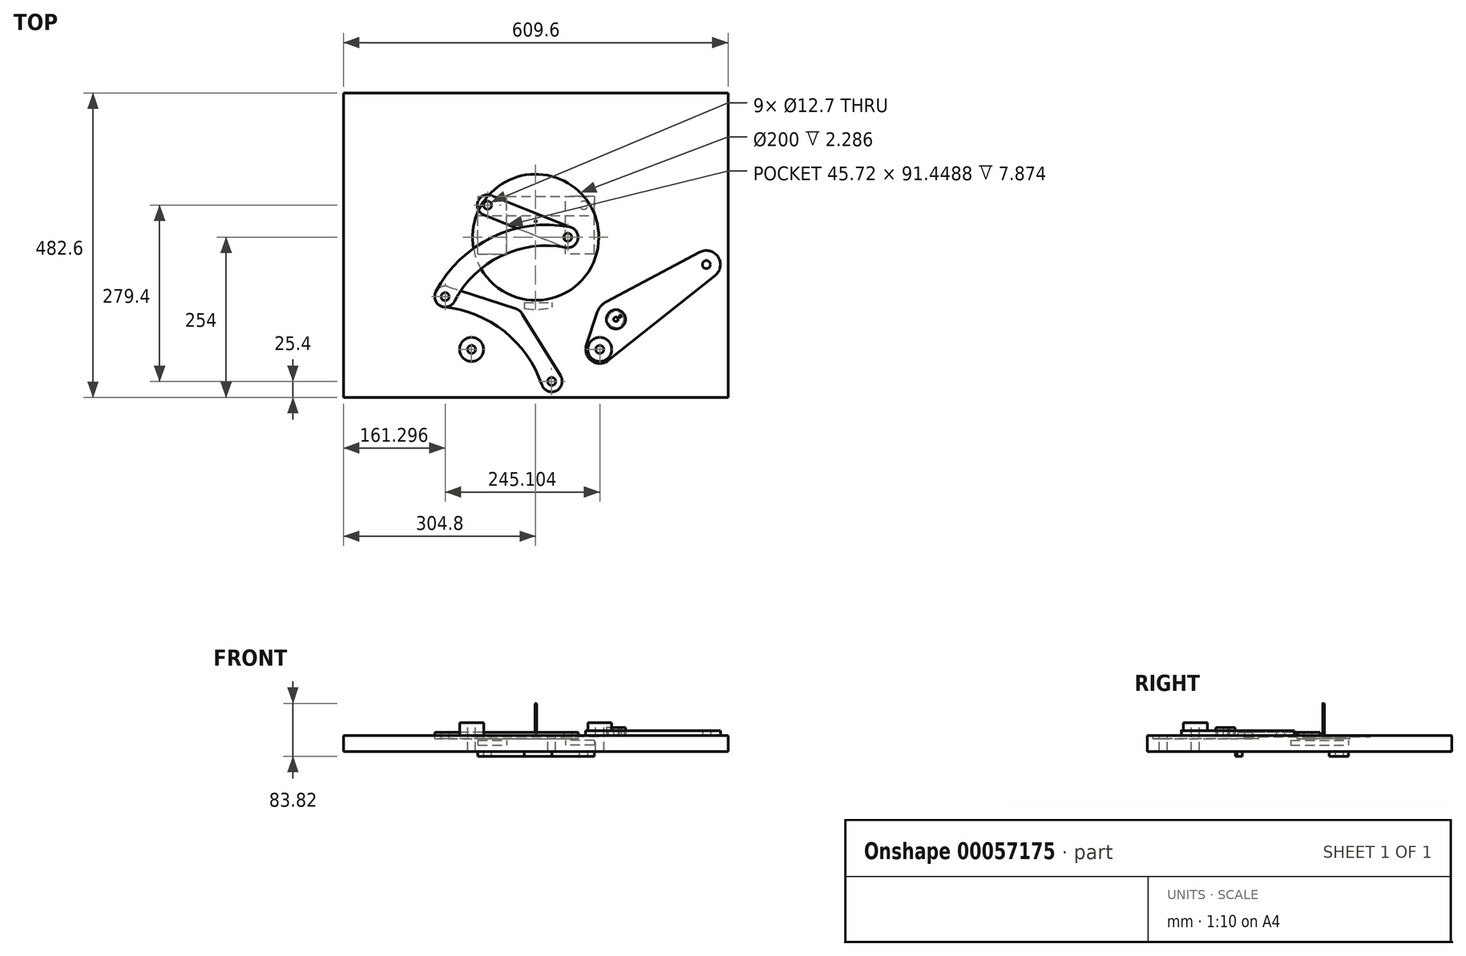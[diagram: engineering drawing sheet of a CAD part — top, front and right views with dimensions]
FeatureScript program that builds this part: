
annotation { "Feature Type Name" : "Feature", "Feature Type Description" : "" }
export const myFeature = defineFeature(function(context is Context, id is Id, definition is map)
    precondition{}
    {
        {
            var Q0;
            Q0=qCreatedBy(makeId("Top.planeOp"),FACE);
            var sketch = newSketch(context, id + "F0", { "sketchPlane" : qUnion([Q0])});
            skCircle(sketch, "E0", {"center": v(0, 0) * mm, "radius": 101.6 * mm, "construction": true});
            skLineSegment(sketch, "E1", {"start": v(-76.2, 50.8) * mm, "end": v(-76.2, 0) * mm, "construction": true});
            skPoint(sketch, "E2", {"position": v(-101.6, -177.8) * mm});
            skCircle(sketch, "E3", {"center": v(-76.2, 50.8) * mm, "radius": 6.35 * mm});
            skLineSegment(sketch, "E4", {"start": v(0, 0) * mm, "end": v(50.8, 0) * mm, "construction": true});
            skCircle(sketch, "E5", {"center": v(50.8, 0) * mm, "radius": 6.35 * mm});
            skPoint(sketch, "E6", {"position": v(25.4, -228.6) * mm});
            skCircle(sketch, "E7", {"center": v(-101.6, -177.8) * mm, "radius": 6.35 * mm});
            skCircle(sketch, "E8", {"center": v(25.4, -228.6) * mm, "radius": 6.35 * mm});
            skLineSegment(sketch, "E9", {"start": v(0, 0) * mm, "end": v(0, 167.48) * mm, "construction": true});
            skCircle(sketch, "E10.MirrorC", {"center": v(76.2, 50.8) * mm, "radius": 6.35 * mm});
            skCircle(sketch, "E11.MirrorC", {"center": v(-50.8, 0) * mm, "radius": 6.35 * mm});
            skCircle(sketch, "E12.MirrorC", {"center": v(101.6, -177.8) * mm, "radius": 6.35 * mm});
            skLineSegment(sketch, "E13", {"start": v(-76.2, 50.8) * mm, "end": v(-270.5, -43.32) * mm});
            skLineSegment(sketch, "E14", {"start": v(-270.5, -43.32) * mm, "end": v(-101.6, -177.8) * mm});
            skLineSegment(sketch, "E15", {"start": v(76.2, 50.8) * mm, "end": v(270.5, -43.32) * mm});
            skLineSegment(sketch, "E16", {"start": v(270.5, -43.32) * mm, "end": v(101.6, -177.8) * mm});
            skLineSegment(sketch, "E17", {"start": v(50.8, 0) * mm, "end": v(-143.5, -94.12) * mm});
            skLineSegment(sketch, "E18", {"start": v(-143.5, -94.12) * mm, "end": v(25.4, -228.6) * mm});
            skArc(sketch, "E19", {"start": v(133.35, 23.12) * mm, "mid": v(131.45, -105.68) * mm, "end": v(228.9, -189.93) * mm});
            skLineSegment(sketch, "E20", {"start": v(270.5, -43.32) * mm, "end": v(228.9, -189.93) * mm});
            skCircle(sketch, "E21", {"center": v(127.1, -130.13) * mm, "radius": 15.24 * mm});
            skLineSegment(sketch, "E22", {"start": v(270.5, -43.32) * mm, "end": v(127.1, -130.13) * mm, "construction": true});
            skLineSegment(sketch, "E23", {"start": v(127.1, -130.13) * mm, "end": v(101.6, -177.8) * mm, "construction": true});
            skLineSegment(sketch, "E24", {"start": v(-76.2, 50.8) * mm, "end": v(50.8, 0) * mm});
            skSolve(sketch);
        }
        {
            var Q0;
            Q0=qCreatedBy(makeId("Top.planeOp"),FACE);
            var sketch = newSketch(context, id + "F1", { "sketchPlane" : qUnion([Q0])});
            skCircle(sketch, "E25", {"center": v(76.2, 50.8) * mm, "radius": 22.23 * mm});
            skCircle(sketch, "E26", {"center": v(270.5, -43.32) * mm, "radius": 22.23 * mm});
            skLineSegment(sketch, "E27", {"start": v(85.89, 70.8) * mm, "end": v(280.2, -23.32) * mm});
            skLineSegment(sketch, "E28", {"start": v(291.88, -49.4) * mm, "end": v(250.72, -194.43) * mm});
            skArc(sketch, "E29", {"start": v(120.43, -16.82) * mm, "mid": v(147.62, -133.46) * mm, "end": v(250.72, -194.43) * mm});
            skLineSegment(sketch, "E30", {"start": v(61.66, 33.99) * mm, "end": v(120.43, -16.82) * mm});
            skCircle(sketch, "E31", {"center": v(270.5, -43.32) * mm, "radius": 6.35 * mm});
            skCircle(sketch, "E32", {"center": v(76.2, 50.8) * mm, "radius": 6.35 * mm});
            skSolve(sketch);
        }
        {
            var Q0;
            Q0=qCreatedBy(makeId("Top.planeOp"),FACE);
            var sketch = newSketch(context, id + "F2", { "sketchPlane" : qUnion([Q0])});
            skCircle(sketch, "E33", {"center": v(270.5, -43.32) * mm, "radius": 22.23 * mm});
            skCircle(sketch, "E34", {"center": v(101.6, -177.8) * mm, "radius": 22.23 * mm});
            skCircle(sketch, "E35", {"center": v(127.1, -130.13) * mm, "radius": 31.75 * mm});
            skLineSegment(sketch, "E36", {"start": v(260.1, -23.69) * mm, "end": v(112.22, -102.08) * mm});
            skLineSegment(sketch, "E37", {"start": v(284.35, -60.7) * mm, "end": v(115.44, -195.19) * mm});
            skLineSegment(sketch, "E38", {"start": v(96.9, -120.33) * mm, "end": v(80.46, -170.94) * mm});
            skCircle(sketch, "E39", {"center": v(270.5, -43.32) * mm, "radius": 6.35 * mm});
            skCircle(sketch, "E40", {"center": v(101.6, -177.8) * mm, "radius": 6.35 * mm});
            skCircle(sketch, "E41", {"center": v(127.1, -130.13) * mm, "radius": 12.7 * mm});
            skSolve(sketch);
        }
        {
            var Q0;
            Q0=qCreatedBy(makeId("Top.planeOp"),FACE);
            var sketch = newSketch(context, id + "F3", { "sketchPlane" : qUnion([Q0])});
            skCircle(sketch, "E42", {"center": v(0, 0) * mm, "radius": 114.3 * mm});
            skCircle(sketch, "E43", {"center": v(-76.2, 50.8) * mm, "radius": 12.31 * mm});
            skCircle(sketch, "E44", {"center": v(76.2, 50.8) * mm, "radius": 11.5 * mm});
            skCircle(sketch, "E45", {"center": v(50.8, 0) * mm, "radius": 12.94 * mm});
            skCircle(sketch, "E46", {"center": v(-6.87, -69.38) * mm, "radius": 23.76 * mm});
            skLineSegment(sketch, "E47", {"start": v(0, 0) * mm, "end": v(0, 183.03) * mm});
            skCircle(sketch, "E48", {"center": v(-76.2, 50.8) * mm, "radius": 6.35 * mm});
            skCircle(sketch, "E49", {"center": v(76.2, 50.8) * mm, "radius": 6.54 * mm});
            skCircle(sketch, "E50", {"center": v(50.8, 0) * mm, "radius": 6.35 * mm});
            skSolve(sketch);
        }
        {
            var Q0;
            Q0=qCreatedBy(makeId("Top.planeOp"),FACE);
            var sketch = newSketch(context, id + "F4", { "sketchPlane" : qUnion([Q0])});
            skCircle(sketch, "E51", {"center": v(-143.5, -94.12) * mm, "radius": 16.51 * mm});
            skCircle(sketch, "E52", {"center": v(50.8, 0) * mm, "radius": 16.51 * mm});
            skCircle(sketch, "E53", {"center": v(-143.5, -94.12) * mm, "radius": 6.35 * mm});
            skCircle(sketch, "E54", {"center": v(50.8, 0) * mm, "radius": 6.35 * mm});
            skArc(sketch, "E55", {"start": v(47.7, -16.22) * mm, "mid": v(-54.75, -29.72) * mm, "end": v(-128.86, -101.74) * mm});
            skArc(sketch, "E56", {"start": v(53.9, 16.22) * mm, "mid": v(-69.15, 0) * mm, "end": v(-158.15, -86.5) * mm});
            skSolve(sketch);
        }
        {
            var Q0;
            Q0=qCreatedBy(makeId("Top.planeOp"),FACE);
            var sketch = newSketch(context, id + "F5", { "sketchPlane" : qUnion([Q0])});
            skCircle(sketch, "E57", {"center": v(-143.5, -94.12) * mm, "radius": 16.51 * mm});
            skCircle(sketch, "E58", {"center": v(-38.47, -132.3) * mm, "radius": 20.32 * mm});
            skCircle(sketch, "E59", {"center": v(25.4, -228.6) * mm, "radius": 16.51 * mm});
            skLineSegment(sketch, "E60", {"start": v(-138.4, -78.42) * mm, "end": v(-32.18, -112.97) * mm});
            skArc(sketch, "E61", {"start": v(9.76, -233.89) * mm, "mid": v(-49.55, -149.43) * mm, "end": v(-145.15, -110.55) * mm});
            skLineSegment(sketch, "E62", {"start": v(-21.17, -121.63) * mm, "end": v(39.45, -219.93) * mm});
            skCircle(sketch, "E63", {"center": v(-143.5, -94.12) * mm, "radius": 6.35 * mm});
            skCircle(sketch, "E64", {"center": v(25.4, -228.6) * mm, "radius": 6.35 * mm});
            skLineSegment(sketch, "E65", {"start": v(-143.5, -94.12) * mm, "end": v(-38.47, -132.3) * mm});
            skSolve(sketch);
        }
        {
            var Q0;
            Q0=qCreatedBy(makeId("Top.planeOp"),FACE);
            var sketch = newSketch(context, id + "F6", { "sketchPlane" : qUnion([Q0])});
            skLineSegment(sketch, "E66.bottom", {"start": v(-304.8, 228.6) * mm, "end": v(304.8, 228.6) * mm});
            skLineSegment(sketch, "E66.top", {"start": v(-304.8, -254) * mm, "end": v(304.8, -254) * mm});
            skLineSegment(sketch, "E66.left", {"start": v(-304.8, 228.6) * mm, "end": v(-304.8, -254) * mm});
            skLineSegment(sketch, "E66.right", {"start": v(304.8, 228.6) * mm, "end": v(304.8, -254) * mm});
            skCircle(sketch, "E67", {"center": v(-101.6, -177.8) * mm, "radius": 6.35 * mm});
            skCircle(sketch, "E68", {"center": v(25.4, -228.6) * mm, "radius": 6.35 * mm});
            skCircle(sketch, "E69", {"center": v(101.6, -177.8) * mm, "radius": 6.35 * mm});
            skSolve(sketch);
        }
        {
            var Q0;
            {var subQ2=sQuery(id+"F1.wireOp",EDGE,"E27");Q0=makeQuery(id+"F1.imprint","IMPRINT",FACE,{"disambiguationData":[TD([[makeQuery(id+"F1.imprint","IMPRINT",EDGE,{"derivedFrom":subQ2}),-1.0]])]});}
            var Q1;
            Q1=makeQuery(id+"F1.imprint","IMPRINT",FACE,{"disambiguationData":[TD([[makeQuery(id+"F1.imprint","IMPRINT",EDGE,{"derivedFrom":sQuery(id+"F1.wireOp",EDGE,"E31")}),-1.0]])]});
            var Q2;
            Q2=makeQuery(id+"F1.imprint","IMPRINT",FACE,{"disambiguationData":[TD([[makeQuery(id+"F1.imprint","IMPRINT",EDGE,{"derivedFrom":sQuery(id+"F1.wireOp",EDGE,"E32")}),-1.0]])]});
            extrude(context, id + "F7", {"entities" : qUnion([Q0, Q1, Q2]), "oppositeDirection" : true, "depth" : 10.16 * mm});
        }
        {
            var Q0;
            Q0=makeQuery(id+"F2.imprint","IMPRINT",FACE,{"disambiguationData":[TD([[makeQuery(id+"F2.imprint","IMPRINT",EDGE,{"derivedFrom":sQuery(id+"F2.wireOp",EDGE,"E41")}),-1.0]])]});
            var Q1;
            {var subQ0=sQuery(id+"F2.wireOp",EDGE,"E35");var subQ1=sQuery(id+"F2.wireOp",EDGE,"E34");var subQ3=makeQuery(id+"F2.imprint","INTERSECT",VERTEX,{"disambiguationData":[OD(0.0)],"derivedFrom":[subQ1,subQ0]});Q1=makeQuery(id+"F2.imprint","IMPRINT",FACE,{"disambiguationData":[TD([[makeQuery(id+"F2.imprint","IMPRINT",EDGE,{"disambiguationData":[TD([[subQ3,1.0]])],"derivedFrom":subQ1}),1.0]])]});}
            var Q2;
            Q2=makeQuery(id+"F2.imprint","IMPRINT",FACE,{"disambiguationData":[TD([[makeQuery(id+"F2.imprint","IMPRINT",EDGE,{"derivedFrom":sQuery(id+"F2.wireOp",EDGE,"E40")}),-1.0]])]});
            var Q3;
            {var subQ0=sQuery(id+"F2.wireOp",EDGE,"E38");Q3=makeQuery(id+"F2.imprint","IMPRINT",FACE,{"disambiguationData":[TD([[makeQuery(id+"F2.imprint","IMPRINT",EDGE,{"derivedFrom":subQ0}),1.0]])]});}
            var Q4;
            {var subQ1=sQuery(id+"F2.wireOp",EDGE,"E36");Q4=makeQuery(id+"F2.imprint","IMPRINT",FACE,{"disambiguationData":[TD([[makeQuery(id+"F2.imprint","IMPRINT",EDGE,{"derivedFrom":subQ1}),1.0]])]});}
            var Q5;
            Q5=makeQuery(id+"F2.imprint","IMPRINT",FACE,{"disambiguationData":[TD([[makeQuery(id+"F2.imprint","IMPRINT",EDGE,{"derivedFrom":sQuery(id+"F2.wireOp",EDGE,"E39")}),-1.0]])]});
            extrude(context, id + "F8", {"entities" : qUnion([Q0, Q1, Q2, Q3, Q4, Q5]), "depth" : 7.62 * mm});
        }
        {
            var Q0;
            Q0=makeQuery(id+"F3.imprint","IMPRINT",FACE,{"disambiguationData":[TD([[makeQuery(id+"F3.imprint","IMPRINT",EDGE,{"derivedFrom":sQuery(id+"F3.wireOp",EDGE,"E42")}),1.0]])]});
            var Q1;
            Q1=makeQuery(id+"F3.imprint","IMPRINT",FACE,{"disambiguationData":[TD([[makeQuery(id+"F3.imprint","IMPRINT",EDGE,{"derivedFrom":sQuery(id+"F3.wireOp",EDGE,"E43")}),1.0]])]});
            var Q2;
            Q2=makeQuery(id+"F3.imprint","IMPRINT",FACE,{"disambiguationData":[TD([[makeQuery(id+"F3.imprint","IMPRINT",EDGE,{"derivedFrom":sQuery(id+"F3.wireOp",EDGE,"E44")}),1.0]])]});
            var Q3;
            Q3=makeQuery(id+"F3.imprint","IMPRINT",FACE,{"disambiguationData":[TD([[makeQuery(id+"F3.imprint","IMPRINT",EDGE,{"derivedFrom":sQuery(id+"F3.wireOp",EDGE,"E45")}),1.0]])]});
            var Q4;
            Q4=makeQuery(id+"F3.imprint","IMPRINT",FACE,{"disambiguationData":[TD([[makeQuery(id+"F3.imprint","IMPRINT",EDGE,{"derivedFrom":sQuery(id+"F3.wireOp",EDGE,"E46")}),1.0]])]});
            extrude(context, id + "F9", {"entities" : qUnion([Q0, Q1, Q2, Q3, Q4]), "oppositeDirection" : true, "depth" : 5.08 * mm});
        }
        {
            var Q0;
            Q0=makeQuery(id+"F4.imprint","IMPRINT",FACE,{"disambiguationData":[TD([[makeQuery(id+"F4.imprint","IMPRINT",EDGE,{"derivedFrom":sQuery(id+"F4.wireOp",EDGE,"E53")}),-1.0]])]});
            var Q1;
            {var subQ1=sQuery(id+"F4.wireOp",EDGE,"cb505705-815a-4a87-8d78-4f1fd2e18b2e");Q1=makeQuery(id+"F4.imprint","IMPRINT",FACE,{"disambiguationData":[TD([[makeQuery(id+"F4.imprint","IMPRINT",EDGE,{"derivedFrom":subQ1}),-1.0]])]});}
            var Q2;
            Q2=makeQuery(id+"F4.imprint","IMPRINT",FACE,{"disambiguationData":[TD([[makeQuery(id+"F4.imprint","IMPRINT",EDGE,{"derivedFrom":sQuery(id+"F4.wireOp",EDGE,"E54")}),-1.0]])]});
            var Q3;
            {var subQ1=sQuery(id+"F4.wireOp",EDGE,"E55");Q3=makeQuery(id+"F4.imprint","IMPRINT",FACE,{"disambiguationData":[TD([[makeQuery(id+"F4.imprint","IMPRINT",EDGE,{"derivedFrom":subQ1}),-1.0]])]});}
            extrude(context, id + "F10", {"entities" : qUnion([Q0, Q1, Q2, Q3]), "depth" : 5.08 * mm});
        }
        {
            var Q0;
            Q0=makeQuery(id+"F5.imprint","IMPRINT",FACE,{"disambiguationData":[TD([[makeQuery(id+"F5.imprint","IMPRINT",EDGE,{"derivedFrom":sQuery(id+"F5.wireOp",EDGE,"E63")}),-1.0]])]});
            var Q1;
            {var subQ5=sQuery(id+"F5.wireOp",EDGE,"E60");Q1=makeQuery(id+"F5.imprint","IMPRINT",FACE,{"disambiguationData":[TD([[makeQuery(id+"F5.imprint","IMPRINT",EDGE,{"derivedFrom":subQ5}),-1.0]])]});}
            var Q2;
            {var subQ3=sQuery(id+"F5.wireOp",EDGE,"E57");var subQ5=sQuery(id+"F5.wireOp",EDGE,"E61");var subQ7=makeQuery(id+"F5.imprint","INTERSECT",VERTEX,{"derivedFrom":[subQ3,subQ5]});Q2=makeQuery(id+"F5.imprint","IMPRINT",FACE,{"disambiguationData":[TD([[makeQuery(id+"F5.imprint","IMPRINT",EDGE,{"disambiguationData":[TD([[subQ7,-1.0]])],"derivedFrom":subQ3}),-1.0]])]});}
            var Q3;
            {var subQ0=sQuery(id+"F5.wireOp",EDGE,"E58");var subQ4=makeQuery(id+"F5.imprint","INTERSECT",VERTEX,{"derivedFrom":[subQ0,sQuery(id+"F5.wireOp",EDGE,"E60")]});Q3=makeQuery(id+"F5.imprint","IMPRINT",FACE,{"disambiguationData":[TD([[makeQuery(id+"F5.imprint","IMPRINT",EDGE,{"disambiguationData":[TD([[subQ4,1.0]])],"derivedFrom":subQ0}),1.0]])]});}
            var Q4;
            {var subQ0=sQuery(id+"F5.wireOp",EDGE,"E62");Q4=makeQuery(id+"F5.imprint","IMPRINT",FACE,{"disambiguationData":[TD([[makeQuery(id+"F5.imprint","IMPRINT",EDGE,{"derivedFrom":subQ0}),-1.0]])]});}
            var Q5;
            Q5=makeQuery(id+"F5.imprint","IMPRINT",FACE,{"disambiguationData":[TD([[makeQuery(id+"F5.imprint","IMPRINT",EDGE,{"derivedFrom":sQuery(id+"F5.wireOp",EDGE,"E64")}),-1.0]])]});
            extrude(context, id + "F11", {"entities" : qUnion([Q0, Q1, Q2, Q3, Q4, Q5]), "oppositeDirection" : true, "depth" : 5.08 * mm});
        }
        {
            var Q0;
            Q0=makeQuery(id+"F6.imprint","IMPRINT",FACE,{"disambiguationData":[TD([[makeQuery(id+"F6.imprint","IMPRINT",EDGE,{"derivedFrom":sQuery(id+"F6.wireOp",EDGE,"E66.bottom")}),-1.0]])]});
            extrude(context, id + "F12", {"entities" : qUnion([Q0]), "oppositeDirection" : true, "depth" : 25.4 * mm});
        }
        {
            var Q0;
            Q0=makeQuery(id+"F9.opExtrude","CAP_FACE",FACE,{"disambiguationData":[OSD([sQuery(id+"F3.wireOp",EDGE,"E42"),sQuery(id+"F3.wireOp",EDGE,"E43"),sQuery(id+"F3.wireOp",EDGE,"E44"),sQuery(id+"F3.wireOp",EDGE,"E45"),sQuery(id+"F3.wireOp",EDGE,"E46")])],"isStart":true});
            var sketch = newSketch(context, id + "F13", { "sketchPlane" : qUnion([Q0])});
            skLineSegment(sketch, "E70.bottom", {"start": v(-91.79, 64.75) * mm, "end": v(92.99, 64.75) * mm});
            skLineSegment(sketch, "E70.top", {"start": v(-91.79, 34.4) * mm, "end": v(92.99, 34.4) * mm});
            skLineSegment(sketch, "E70.left", {"start": v(-91.79, 64.75) * mm, "end": v(-91.79, 34.4) * mm});
            skLineSegment(sketch, "E70.right", {"start": v(92.99, 64.75) * mm, "end": v(92.99, 34.4) * mm});
            skLineSegment(sketch, "E71.bottom", {"start": v(-17.88, -103.5) * mm, "end": v(25.69, -103.5) * mm});
            skLineSegment(sketch, "E71.top", {"start": v(-17.88, -127.84) * mm, "end": v(25.69, -127.84) * mm});
            skLineSegment(sketch, "E71.left", {"start": v(-17.88, -103.5) * mm, "end": v(-17.88, -127.84) * mm});
            skLineSegment(sketch, "E71.right", {"start": v(25.69, -103.5) * mm, "end": v(25.69, -127.84) * mm});
            skSolve(sketch);
        }
        {
            var Q0;
            Q0=makeQuery(id+"F13.imprint","IMPRINT",FACE,{"disambiguationData":[TD([[makeQuery(id+"F13.imprint","IMPRINT",EDGE,{"derivedFrom":sQuery(id+"F13.wireOp",EDGE,"E70.bottom")}),-1.0]])]});
            var Q1;
            Q1=makeQuery(id+"F13.imprint","IMPRINT",FACE,{"disambiguationData":[TD([[makeQuery(id+"F13.imprint","IMPRINT",EDGE,{"derivedFrom":sQuery(id+"F13.wireOp",EDGE,"E71.bottom")}),-1.0]])]});
            extrude(context, id + "F14", {"entities" : qUnion([Q0, Q1]), "operationType" : NewBodyOperationType.ADD, "oppositeDirection" : true, "depth" : 33.02 * mm});
        }
        {
            var Q0;
            Q0=makeQuery(id+"F14.opExtrude","SWEPT_FACE",FACE,{"disambiguationData":[OSD([sQuery(id+"F13.wireOp",EDGE,"E70.bottom")])]});
            var sketch = newSketch(context, id + "F15", { "sketchPlane" : qUnion([Q0])});
            skLineSegment(sketch, "E72.bottom", {"start": v(-92.99, -7.62) * mm, "end": v(-47.27, -7.62) * mm});
            skLineSegment(sketch, "E72.top", {"start": v(-92.99, -15.5) * mm, "end": v(-47.27, -15.5) * mm});
            skLineSegment(sketch, "E72.left", {"start": v(-92.99, -7.62) * mm, "end": v(-92.99, -15.5) * mm});
            skLineSegment(sketch, "E72.right", {"start": v(-47.27, -7.62) * mm, "end": v(-47.27, -15.5) * mm});
            skLineSegment(sketch, "E73.bottom", {"start": v(91.79, -7.62) * mm, "end": v(46.07, -7.62) * mm});
            skLineSegment(sketch, "E73.top", {"start": v(91.79, -15.5) * mm, "end": v(46.07, -15.5) * mm});
            skLineSegment(sketch, "E73.left", {"start": v(91.79, -7.62) * mm, "end": v(91.79, -15.5) * mm});
            skLineSegment(sketch, "E73.right", {"start": v(46.07, -7.62) * mm, "end": v(46.07, -15.5) * mm});
            skSolve(sketch);
        }
        {
            var Q0;
            Q0=makeQuery(id+"F15.imprint","IMPRINT",FACE,{"disambiguationData":[TD([[makeQuery(id+"F15.imprint","IMPRINT",EDGE,{"derivedFrom":sQuery(id+"F15.wireOp",EDGE,"E72.bottom")}),-1.0]])]});
            var Q1;
            Q1=makeQuery(id+"F15.imprint","IMPRINT",FACE,{"disambiguationData":[TD([[makeQuery(id+"F15.imprint","IMPRINT",EDGE,{"derivedFrom":sQuery(id+"F15.wireOp",EDGE,"E73.bottom")}),1.0]])]});
            extrude(context, id + "F16", {"entities" : qUnion([Q0, Q1]), "operationType" : NewBodyOperationType.REMOVE, "oppositeDirection" : true, "depth" : 91.45 * mm});
        }
        {
            var Q0;
            Q0=makeQuery(id+"F9.opExtrude","CAP_FACE",FACE,{"disambiguationData":[OSD([sQuery(id+"F3.wireOp",EDGE,"E42"),sQuery(id+"F3.wireOp",EDGE,"E48"),sQuery(id+"F3.wireOp",EDGE,"E49"),sQuery(id+"F3.wireOp",EDGE,"E50")])],"isStart":true});
            var sketch = newSketch(context, id + "F17", { "sketchPlane" : qUnion([Q0])});
            skCircle(sketch, "E74", {"center": v(0, 0) * mm, "radius": 100 * mm});
            skSolve(sketch);
        }
        {
            var Q0;
            Q0=makeQuery(id+"F17.imprint","IMPRINT",FACE,{"disambiguationData":[TD([[makeQuery(id+"F17.imprint","IMPRINT",EDGE,{"derivedFrom":sQuery(id+"F17.wireOp",EDGE,"E74")}),1.0]])]});
            extrude(context, id + "F18", {"entities" : qUnion([Q0]), "operationType" : NewBodyOperationType.REMOVE, "oppositeDirection" : true, "depth" : 2.3 * mm});
        }
        {
            var Q0;
            Q0=makeQuery(id+"F12.opExtrude","CAP_FACE",FACE,{"disambiguationData":[OSD([sQuery(id+"F6.wireOp",EDGE,"E66.bottom"),sQuery(id+"F6.wireOp",EDGE,"E66.top"),sQuery(id+"F6.wireOp",EDGE,"E66.left"),sQuery(id+"F6.wireOp",EDGE,"E66.right"),sQuery(id+"F6.wireOp",EDGE,"E67"),sQuery(id+"F6.wireOp",EDGE,"E68"),sQuery(id+"F6.wireOp",EDGE,"E69")])],"isStart":true});
            var sketch = newSketch(context, id + "F19", { "sketchPlane" : qUnion([Q0])});
            skCircle(sketch, "E75", {"center": v(-101.6, -177.8) * mm, "radius": 19.05 * mm});
            skCircle(sketch, "E76", {"center": v(101.6, -177.8) * mm, "radius": 19.05 * mm});
            skSolve(sketch);
        }
        {
            var Q0;
            Q0=makeQuery(id+"F19.imprint","IMPRINT",FACE,{"disambiguationData":[TD([[makeQuery(id+"F19.imprint","IMPRINT",EDGE,{"derivedFrom":sQuery(id+"F19.wireOp",EDGE,"E75")}),1.0]])]});
            var Q1;
            Q1=makeQuery(id+"F19.imprint","IMPRINT",FACE,{"disambiguationData":[TD([[makeQuery(id+"F19.imprint","IMPRINT",EDGE,{"derivedFrom":sQuery(id+"F19.wireOp",EDGE,"E76")}),1.0]])]});
            extrude(context, id + "F20", {"entities" : qUnion([Q0, Q1]), "operationType" : NewBodyOperationType.ADD, "depth" : 20.32 * mm});
        }
        {
            var Q0;
            Q0=qCreatedBy(makeId("Top.planeOp"),FACE);
            var sketch = newSketch(context, id + "F21", { "sketchPlane" : qUnion([Q0])});
            skCircle(sketch, "E77", {"center": v(-76.2, 50.8) * mm, "radius": 16.51 * mm});
            skCircle(sketch, "E78", {"center": v(50.8, 0) * mm, "radius": 16.51 * mm});
            skLineSegment(sketch, "E79", {"start": v(-70.07, 66.13) * mm, "end": v(56.93, 15.33) * mm});
            skLineSegment(sketch, "E80", {"start": v(-82.33, 35.47) * mm, "end": v(44.67, -15.33) * mm});
            skCircle(sketch, "E81", {"center": v(-76.2, 50.8) * mm, "radius": 6.35 * mm});
            skCircle(sketch, "E82", {"center": v(50.8, 0) * mm, "radius": 6.35 * mm});
            skSolve(sketch);
        }
        {
            var Q0;
            {var subQ1=sQuery(id+"F21.wireOp",EDGE,"E79");Q0=makeQuery(id+"F21.imprint","IMPRINT",FACE,{"disambiguationData":[TD([[makeQuery(id+"F21.imprint","IMPRINT",EDGE,{"derivedFrom":subQ1}),-1.0]])]});}
            var Q1;
            Q1=makeQuery(id+"F21.imprint","IMPRINT",FACE,{"disambiguationData":[TD([[makeQuery(id+"F21.imprint","IMPRINT",EDGE,{"derivedFrom":sQuery(id+"F21.wireOp",EDGE,"E81")}),-1.0]])]});
            var Q2;
            Q2=makeQuery(id+"F21.imprint","IMPRINT",FACE,{"disambiguationData":[TD([[makeQuery(id+"F21.imprint","IMPRINT",EDGE,{"derivedFrom":sQuery(id+"F21.wireOp",EDGE,"E82")}),-1.0]])]});
            extrude(context, id + "F22", {"entities" : qUnion([Q0, Q1, Q2]), "oppositeDirection" : true, "depth" : 5.08 * mm});
        }
        {
            var Q0;
            Q0=makeQuery(id+"F12.opExtrude","CAP_FACE",FACE,{"disambiguationData":[OSD([sQuery(id+"F6.wireOp",EDGE,"E66.bottom"),sQuery(id+"F6.wireOp",EDGE,"E66.top"),sQuery(id+"F6.wireOp",EDGE,"E66.left"),sQuery(id+"F6.wireOp",EDGE,"E66.right"),sQuery(id+"F6.wireOp",EDGE,"E67"),sQuery(id+"F6.wireOp",EDGE,"E68"),sQuery(id+"F6.wireOp",EDGE,"E69")])],"isStart":true});
            var sketch = newSketch(context, id + "F23", { "sketchPlane" : qUnion([Q0])});
            skCircle(sketch, "E83", {"center": v(0, 25.4) * mm, "radius": 1.27 * mm});
            skSolve(sketch);
        }
        {
            var Q0;
            Q0=qSketchRegion(id+"F23",true);
            extrude(context, id + "F24", {"entities" : qUnion([Q0]), "operationType" : NewBodyOperationType.ADD, "depth" : 50.8 * mm});
        }
        {
            var Q0;
            Q0=qCreatedBy(makeId("Top.planeOp"),FACE);
            var sketch = newSketch(context, id + "F25", { "sketchPlane" : qUnion([Q0])});
            skCircle(sketch, "E84", {"center": v(127.1, -130.13) * mm, "radius": 15.24 * mm});
            skCircle(sketch, "E85", {"center": v(127.1, -130.13) * mm, "radius": 3.55 * mm});
            skCircle(sketch, "E86", {"center": v(134.03, -125.52) * mm, "radius": 1.52 * mm});
            skSolve(sketch);
        }
        {
            var Q0;
            Q0=qSketchRegion(id+"F25",true);
            extrude(context, id + "F26", {"entities" : qUnion([Q0]), "depth" : 12.7 * mm});
        }
    });
